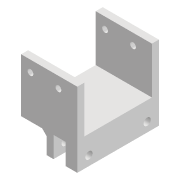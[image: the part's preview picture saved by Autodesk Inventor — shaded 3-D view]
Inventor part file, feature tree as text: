
AUTODESK INVENTOR PART (.ipt)
format: ipt  version: 2022 (Build 260153000, 153)  size: 195,584 bytes
history: native  units: mm
features: extrude x5, sketch x5, thicken_offset x3, chamfer x1, projected_geometry x1
ambient origin geometry x8: Origin, YZ Plane, XZ Plane, XY Plane, X Axis, Y Axis, Z Axis, Center Point
bodies: Solid1 (feature_tree)
feature tree (15):
  extrude  "Extrusion1"  Depth=29.0mm
  extrude  "Extrusion2"  Depth=2.5mm
  extrude  "Extrusion4"  Depth=8.0mm
  extrude  "Extrusion5"  Depth=5.0mm
  extrude  "Extrusion6"  Depth=5.0mm
  thicken_offset  "Thicken1"
  thicken_offset  "Thicken2"
  chamfer  "Chamfer1"  Distance=12.0mm
  thicken_offset  "Thicken3"
  sketch  "Sketch1"  dims[d0=29.0mm d1=14.5mm]
  sketch  "Sketch2"  dims[d3=2.5mm d4=2.5mm]
  sketch  "Sketch5"  dims[d5=16.0mm d6=8.0mm]
  sketch  "Sketch6"  dims[d7=5.0mm d8=5.0mm]
  sketch  "Sketch8"  dims[d9=2.5mm d10=2.5mm d11=12.0mm d12=12.0mm d13=5.0mm d14=3.0mm d15=0.0mm d17=3.0mm d18=9.0mm d19=0.0mm d24=3.0mm d25=3.0mm d26=3.0mm d27=3.0mm d30=20.0mm d31=0.0mm d34=2.5mm d38=50.0mm d39=0.0mm d40=3.0mm d41=5.0mm d42=3.1mm d43=3.1mm d46=4.0mm d47=4.0mm d48=100.0mm d49=0.0mm d50=0.0mm d53=2.5mm d54=4.0mm d55=6.0mm d56=15.25mm d57=15.25mm d58=0.1mm d59=0.1mm d60=0.1mm d61=0.1mm d62=2.0mm d63=2.0mm d64=45.0deg d65=5.0mm d66=5.0mm d67=2.1mm d68=2.1mm]
  projected_geometry  "Projected Loop1"
